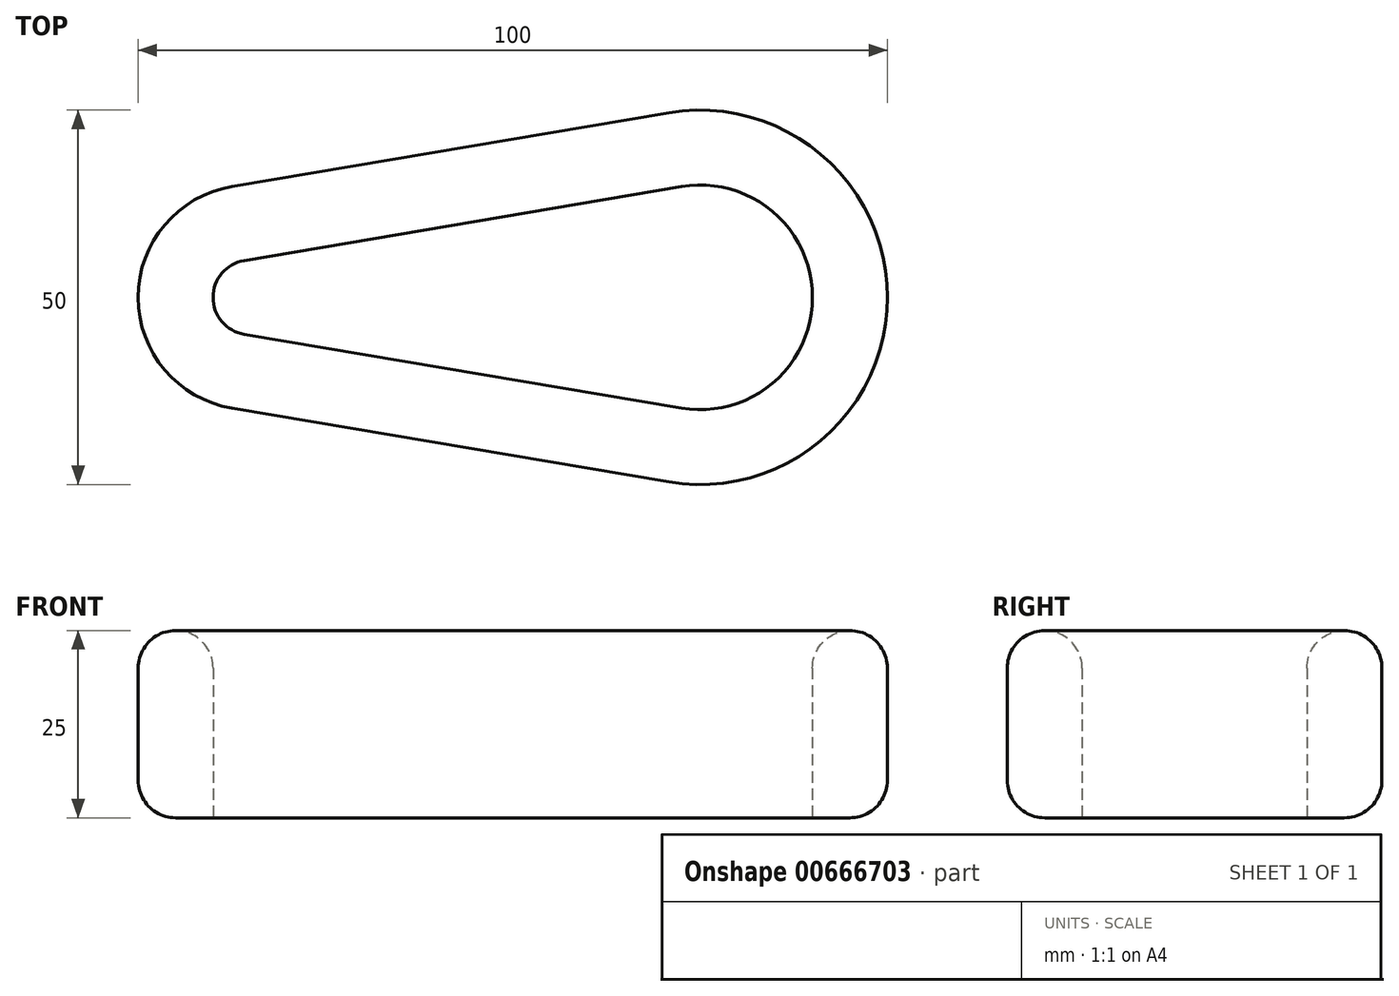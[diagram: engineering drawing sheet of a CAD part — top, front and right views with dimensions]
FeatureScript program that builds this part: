
annotation { "Feature Type Name" : "Feature", "Feature Type Description" : "" }
export const myFeature = defineFeature(function(context is Context, id is Id, definition is map)
    precondition{}
    {
        {
            var Q0;
            Q0=qCreatedBy(makeId("Top.planeOp"),FACE);
            var sketch = newSketch(context, id + "F0", { "sketchPlane" : qUnion([Q0])});
            skArc(sketch, "E0", {"start": v(-62.5, 14.8) * mm, "mid": v(-75, 0) * mm, "end": v(-62.5, -14.8) * mm});
            skArc(sketch, "E1", {"start": v(-4.17, -24.65) * mm, "mid": v(25, 0) * mm, "end": v(-4.17, 24.65) * mm});
            skLineSegment(sketch, "E2", {"start": v(-62.5, -14.8) * mm, "end": v(-4.17, -24.65) * mm});
            skLineSegment(sketch, "E3", {"start": v(-60, 0) * mm, "end": v(0, 0) * mm, "construction": true});
            skLineSegment(sketch, "E4.MirrorCS", {"start": v(-62.5, 14.8) * mm, "end": v(-4.17, 24.65) * mm});
            skPoint(sketch, "E5.orphan", {"position": v(46, 33.13) * mm});
            skPoint(sketch, "E6.orphan", {"position": v(46, -33.13) * mm});
            skPoint(sketch, "E7.orphan", {"position": v(-61.52, -14.96) * mm});
            skPoint(sketch, "E8.orphan", {"position": v(-61.52, 14.96) * mm});
            skLineSegment(sketch, "E9.0", {"start": v(-60.83, 4.93) * mm, "end": v(-2.5, 14.8) * mm});
            skArc(sketch, "E9.1", {"start": v(-60.83, 4.93) * mm, "mid": v(-65, 0) * mm, "end": v(-60.83, -4.93) * mm});
            skLineSegment(sketch, "E9.2", {"start": v(-60.83, -4.93) * mm, "end": v(-2.5, -14.8) * mm});
            skArc(sketch, "E9.3", {"start": v(-2.5, -14.8) * mm, "mid": v(15, 0) * mm, "end": v(-2.5, 14.8) * mm});
            skSolve(sketch);
        }
        {
            var Q0;
            Q0 = qSketchRegion(id + "F0", true);
            extrude(context, id + "F1", {"entities" : qUnion([Q0]), "depth" : 25 * mm, "offsetDistance" : 25 * mm});
        }
        {
            var Q0;
            Q0=makeQuery(id+"F1.opExtrude","CAP_FACE",FACE,{"disambiguationData":[OSD([sQuery(id+"F0.wireOp",EDGE,"E0"),sQuery(id+"F0.wireOp",EDGE,"E1"),sQuery(id+"F0.wireOp",EDGE,"E2"),sQuery(id+"F0.wireOp",EDGE,"E4.MirrorCS"),sQuery(id+"F0.wireOp",EDGE,"E9.0"),sQuery(id+"F0.wireOp",EDGE,"E9.1"),sQuery(id+"F0.wireOp",EDGE,"E9.2"),sQuery(id+"F0.wireOp",EDGE,"E9.3")])],"isStart":false});
            var Q1;
            Q1=makeQuery(id+"F1.opExtrude","SWEPT_FACE",FACE,{"disambiguationData":[OSD([sQuery(id+"F0.wireOp",EDGE,"E1")])]});
            fillet(context, id + "F2", {"entities" : qUnion([Q0, Q1]), "radius" : 5 * mm, "tangentPropagation" : true, "allowEdgeOverflow" : false});
        }
    });
